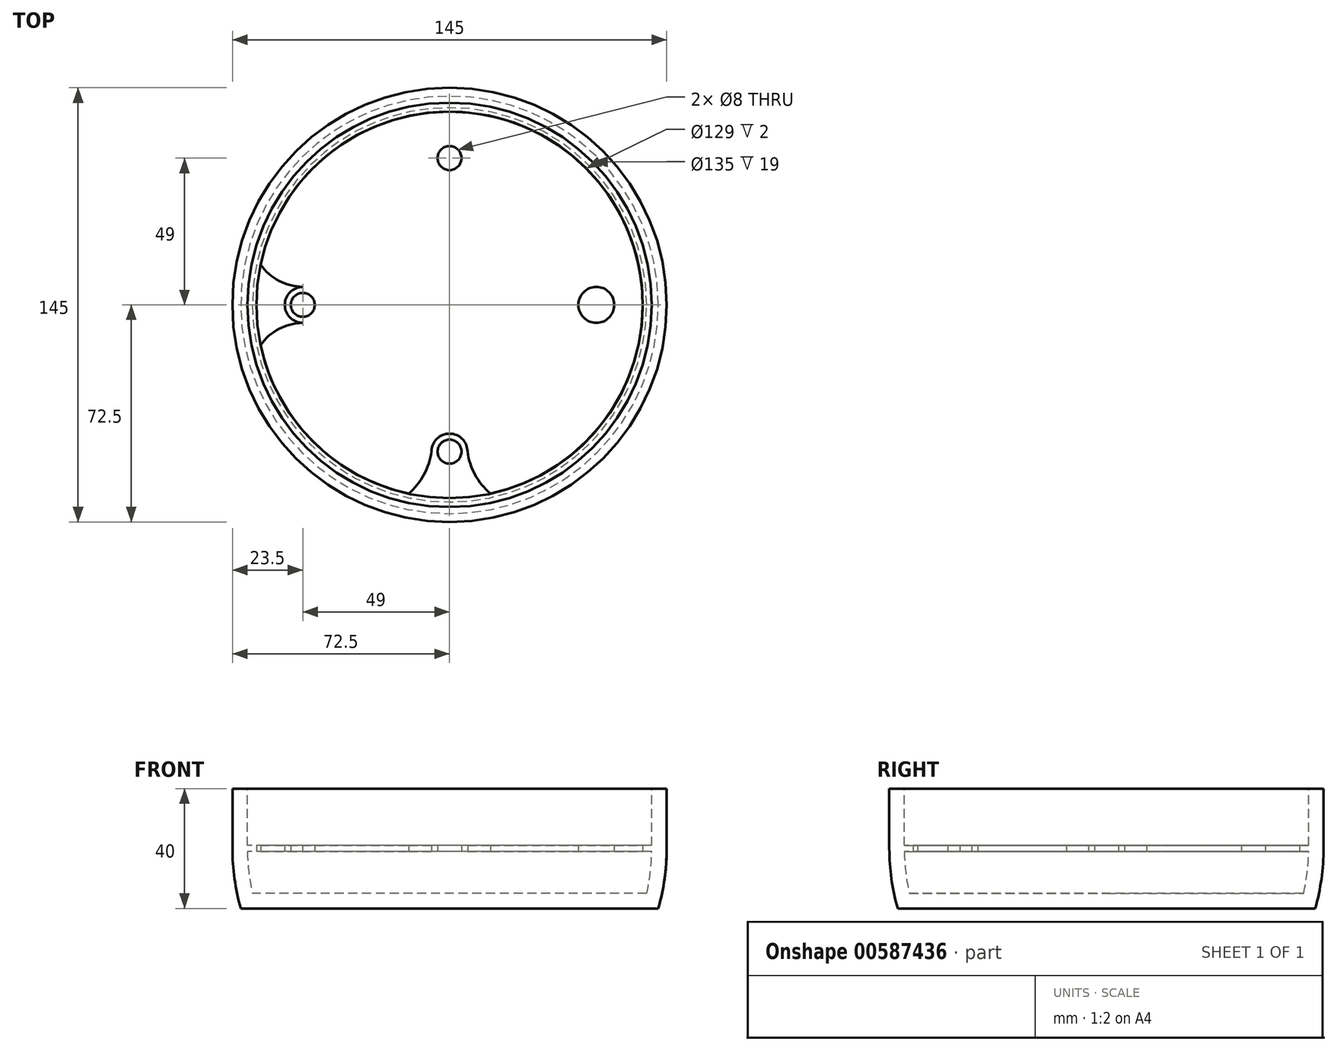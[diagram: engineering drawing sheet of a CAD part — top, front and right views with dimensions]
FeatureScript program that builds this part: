
annotation { "Feature Type Name" : "Feature", "Feature Type Description" : "" }
export const myFeature = defineFeature(function(context is Context, id is Id, definition is map)
    precondition{}
    {
        {
            var Q0;
            Q0=qCreatedBy(makeId("Top.planeOp"),FACE);
            var sketch = newSketch(context, id + "F0", { "sketchPlane" : qUnion([Q0])});
            skCircle(sketch, "E0", {"center": v(0, 0) * mm, "radius": 67.5 * mm});
            skCircle(sketch, "E1.0", {"center": v(0, 0) * mm, "radius": 64.5 * mm});
            skCircle(sketch, "E2", {"center": v(0, 49) * mm, "radius": 4 * mm});
            skCircle(sketch, "E3.0", {"center": v(0, 49) * mm, "radius": 6 * mm});
            skCircle(sketch, "E4.MirrorC", {"center": v(0, -49) * mm, "radius": 4 * mm});
            skCircle(sketch, "E5.MirrorC", {"center": v(0, -49) * mm, "radius": 6 * mm});
            skCircle(sketch, "E6", {"center": v(-49, 0) * mm, "radius": 4 * mm});
            skCircle(sketch, "E7.0", {"center": v(-49, 0) * mm, "radius": 6 * mm});
            skCircle(sketch, "E8.MirrorC", {"center": v(49, 0) * mm, "radius": 6 * mm});
            skCircle(sketch, "E9.MirrorC", {"center": v(49, 0) * mm, "radius": 4 * mm});
            skArc(sketch, "E10.MirrorCS", {"start": v(13.67, 63.03) * mm, "mid": v(8.52, 56.67) * mm, "end": v(6, 48.88) * mm});
            skArc(sketch, "E11.MirrorCS", {"start": v(-13.67, 63.03) * mm, "mid": v(-8.52, 56.67) * mm, "end": v(-6, 48.88) * mm});
            skArc(sketch, "E12", {"start": v(-63.09, 13.43) * mm, "mid": v(-56.97, 8.03) * mm, "end": v(-49.08, 6) * mm});
            skArc(sketch, "E13.MirrorCS", {"start": v(-63.09, -13.43) * mm, "mid": v(-56.97, -8.03) * mm, "end": v(-49.08, -6) * mm});
            skArc(sketch, "E14.MirrorCS", {"start": v(13.67, -63.03) * mm, "mid": v(8.52, -56.67) * mm, "end": v(6, -48.88) * mm});
            skArc(sketch, "E15.MirrorCS", {"start": v(-13.67, -63.03) * mm, "mid": v(-8.52, -56.67) * mm, "end": v(-6, -48.88) * mm});
            skArc(sketch, "E16.MirrorCS", {"start": v(63.09, -13.43) * mm, "mid": v(56.97, -8.03) * mm, "end": v(49.08, -6) * mm});
            skArc(sketch, "E17.MirrorCS", {"start": v(63.09, 13.43) * mm, "mid": v(56.97, 8.03) * mm, "end": v(49.08, 6) * mm});
            skSolve(sketch);
        }
        {
            var Q0;
            {var subQ0=sQuery(id+"F0.wireOp",EDGE,"E13.MirrorCS");Q0=makeQuery(id+"F0.imprint","IMPRINT",FACE,{"disambiguationData":[TD([[makeQuery(id+"F0.imprint","IMPRINT",EDGE,{"derivedFrom":subQ0}),1.0]])]});}
            var Q1;
            {var subQ0=sQuery(id+"F0.wireOp",EDGE,"E14.MirrorCS");Q1=makeQuery(id+"F0.imprint","IMPRINT",FACE,{"disambiguationData":[TD([[makeQuery(id+"F0.imprint","IMPRINT",EDGE,{"derivedFrom":subQ0}),1.0]])]});}
            var Q2;
            {var subQ0=sQuery(id+"F0.wireOp",EDGE,"E10.MirrorCS");Q2=makeQuery(id+"F0.imprint","IMPRINT",FACE,{"disambiguationData":[TD([[makeQuery(id+"F0.imprint","IMPRINT",EDGE,{"derivedFrom":subQ0}),-1.0]])]});}
            var Q3;
            {var subQ0=sQuery(id+"F0.wireOp",EDGE,"E16.MirrorCS");Q3=makeQuery(id+"F0.imprint","IMPRINT",FACE,{"disambiguationData":[TD([[makeQuery(id+"F0.imprint","IMPRINT",EDGE,{"derivedFrom":subQ0}),-1.0]])]});}
            var Q4;
            Q4=makeQuery(id+"F0.imprint","IMPRINT",FACE,{"disambiguationData":[TD([[makeQuery(id+"F0.imprint","IMPRINT",EDGE,{"derivedFrom":sQuery(id+"F0.wireOp",EDGE,"E9.MirrorC")}),1.0]])]});
            var Q5;
            Q5=makeQuery(id+"F0.imprint","IMPRINT",FACE,{"disambiguationData":[TD([[makeQuery(id+"F0.imprint","IMPRINT",EDGE,{"derivedFrom":sQuery(id+"F0.wireOp",EDGE,"E6")}),-1.0]])]});
            var Q6;
            Q6=makeQuery(id+"F0.imprint","IMPRINT",FACE,{"disambiguationData":[TD([[makeQuery(id+"F0.imprint","IMPRINT",EDGE,{"derivedFrom":sQuery(id+"F0.wireOp",EDGE,"E4.MirrorC")}),1.0]])]});
            var Q7;
            Q7=makeQuery(id+"F0.imprint","IMPRINT",FACE,{"disambiguationData":[TD([[makeQuery(id+"F0.imprint","IMPRINT",EDGE,{"derivedFrom":sQuery(id+"F0.wireOp",EDGE,"E2")}),-1.0]])]});
            extrude(context, id + "F1", {"entities" : qUnion([Q0, Q1, Q2, Q3, Q4, Q5, Q6, Q7]), "endBound" : BoundingType.SYMMETRIC, "depth" : 2 * mm, "offsetDistance" : 25 * mm});
        }
        {
            var Q0;
            Q0=qCreatedBy(makeId("Front.planeOp"),FACE);
            var sketch = newSketch(context, id + "F2", { "sketchPlane" : qUnion([Q0])});
            skLineSegment(sketch, "E18", {"start": v(0, 30) * mm, "end": v(0, -15) * mm});
            skLineSegment(sketch, "E19", {"start": v(-65.81, -15) * mm, "end": v(0, -15) * mm});
            skArc(sketch, "E20", {"start": v(-67.5, 0) * mm, "mid": v(-67.08, -7.55) * mm, "end": v(-65.81, -15) * mm});
            skLineSegment(sketch, "E21", {"start": v(-67.5, 0) * mm, "end": v(-67.5, 20) * mm});
            skLineSegment(sketch, "E22.0", {"start": v(-72.5, 0) * mm, "end": v(-72.5, 20) * mm});
            skArc(sketch, "E22.1", {"start": v(-72.5, 0) * mm, "mid": v(-71.8, -10.1) * mm, "end": v(-69.69, -20) * mm});
            skLineSegment(sketch, "E22.2", {"start": v(-69.69, -20) * mm, "end": v(0, -20) * mm});
            skLineSegment(sketch, "E23", {"start": v(-72.5, 20) * mm, "end": v(-67.5, 20) * mm});
            skLineSegment(sketch, "E24", {"start": v(0, -20) * mm, "end": v(0, -15) * mm});
            skArc(sketch, "E25", {"start": v(-52.98, -0.9) * mm, "mid": v(-61.35, -4.11) * mm, "end": v(-66.52, -11.44) * mm});
            skLineSegment(sketch, "E26", {"start": v(-52.98, -0.9) * mm, "end": v(-67.5, -0.9) * mm});
            skSolve(sketch);
        }
        {
            var Q0;
            Q0 = qSketchRegion(id + "F0", true);
            extrude(context, id + "F3", {"entities" : qUnion([Q0]), "endBound" : BoundingType.SYMMETRIC, "depth" : 2 * mm, "offsetDistance" : 25 * mm});
        }
        {
            var Q0;
            Q0=makeQuery(id+"F2.imprint","IMPRINT",FACE,{"disambiguationData":[TD([[makeQuery(id+"F2.imprint","IMPRINT",EDGE,{"derivedFrom":sQuery(id+"F2.wireOp",EDGE,"E19")}),-1.0]])]});
            var Q1;
            Q1=sQuery(id+"F2.wireOp",EDGE,"E18");
            revolve(context, id + "F4", {"operationType" : NewBodyOperationType.ADD, "entities" : qUnion([Q0]), "axis" : qUnion([Q1]), "revolveType" : RevolveType.FULL});
        }
    });
